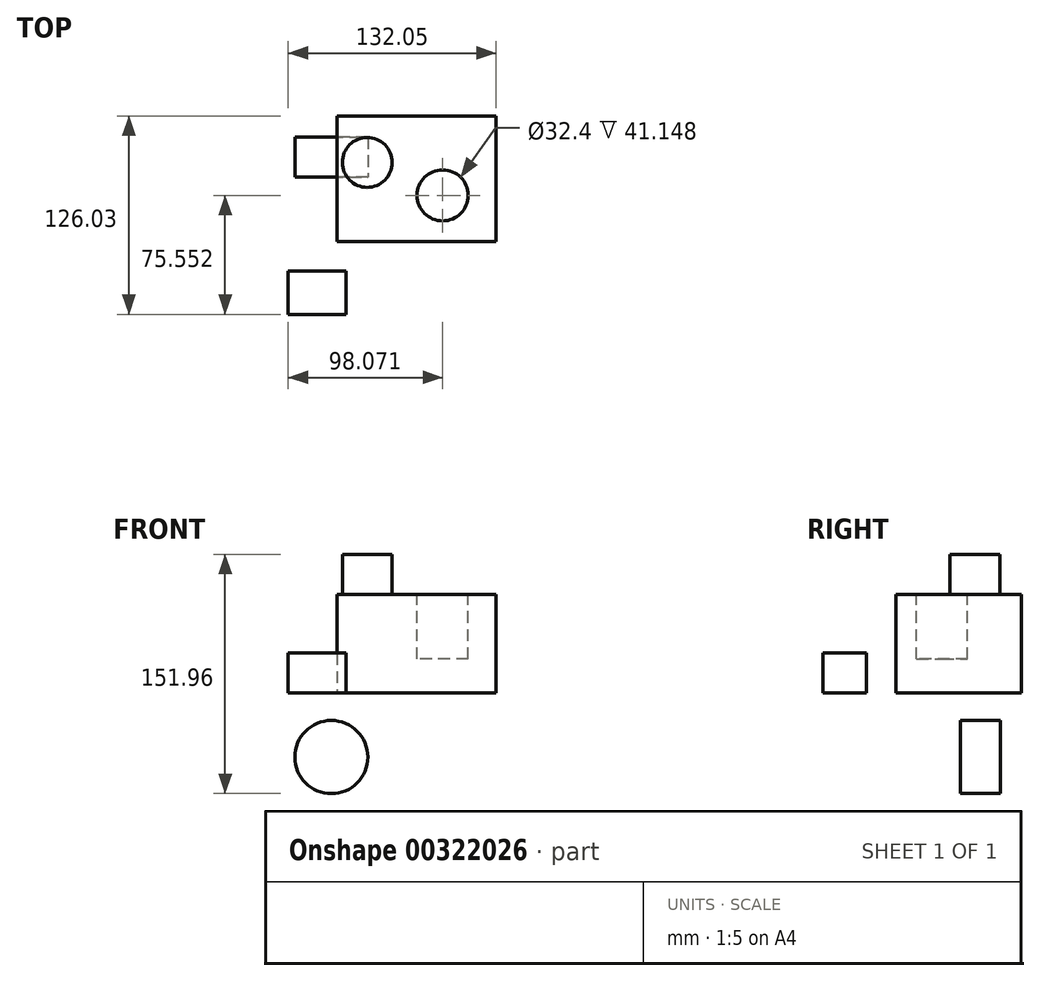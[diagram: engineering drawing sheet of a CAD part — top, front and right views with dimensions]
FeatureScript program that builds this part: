
annotation { "Feature Type Name" : "Feature", "Feature Type Description" : "" }
export const myFeature = defineFeature(function(context is Context, id is Id, definition is map)
    precondition{}
    {
        {
            var Q0;
            Q0=qCreatedBy(makeId("Top.planeOp"),FACE);
            var sketch = newSketch(context, id + "F0", { "sketchPlane" : qUnion([Q0])});
            skLineSegment(sketch, "E0.bottom", {"start": v(-39.24, 38.83) * mm, "end": v(61.89, 38.83) * mm});
            skLineSegment(sketch, "E0.top", {"start": v(-39.24, -40.85) * mm, "end": v(61.89, -40.85) * mm});
            skLineSegment(sketch, "E0.left", {"start": v(-39.24, 38.83) * mm, "end": v(-39.24, -40.85) * mm});
            skLineSegment(sketch, "E0.right", {"start": v(61.89, 38.83) * mm, "end": v(61.89, -40.85) * mm});
            skSolve(sketch);
        }
        {
            var Q0;
            Q0=makeQuery(id+"F0.imprint","IMPRINT",FACE,{"disambiguationData":[TD([[makeQuery(id+"F0.imprint","IMPRINT",EDGE,{"derivedFrom":sQuery(id+"F0.wireOp",EDGE,"E0.bottom")}),-1.0]])]});
            extrude(context, id + "F1", {"entities" : qUnion([Q0]), "depth" : 62.74 * mm});
        }
        {
            var Q0;
            Q0=makeQuery(id+"F1.opExtrude","CAP_FACE",FACE,{"disambiguationData":[OSD([sQuery(id+"F0.wireOp",EDGE,"E0.bottom"),sQuery(id+"F0.wireOp",EDGE,"E0.top"),sQuery(id+"F0.wireOp",EDGE,"E0.left"),sQuery(id+"F0.wireOp",EDGE,"E0.right")])],"isStart":false});
            var sketch = newSketch(context, id + "F2", { "sketchPlane" : qUnion([Q0])});
            skCircle(sketch, "E1", {"center": v(27.91, -11.65) * mm, "radius": 16.2 * mm});
            skSolve(sketch);
        }
        {
            var Q0;
            Q0=makeQuery(id+"F2.imprint","IMPRINT",FACE,{"disambiguationData":[TD([[makeQuery(id+"F2.imprint","IMPRINT",EDGE,{"derivedFrom":sQuery(id+"F2.wireOp",EDGE,"E1")}),1.0]])]});
            extrude(context, id + "F3", {"entities" : qUnion([Q0]), "operationType" : NewBodyOperationType.REMOVE, "oppositeDirection" : true, "depth" : 41.15 * mm});
        }
        {
            var Q0;
            Q0=qCreatedBy(makeId("Top.planeOp"),FACE);
            var sketch = newSketch(context, id + "F4", { "sketchPlane" : qUnion([Q0])});
            skLineSegment(sketch, "E2.bottom", {"start": v(-70.16, -87.2) * mm, "end": v(-33.46, -87.2) * mm});
            skLineSegment(sketch, "E2.top", {"start": v(-70.16, -59.59) * mm, "end": v(-33.46, -59.59) * mm});
            skLineSegment(sketch, "E2.left", {"start": v(-70.16, -87.2) * mm, "end": v(-70.16, -59.59) * mm});
            skLineSegment(sketch, "E2.right", {"start": v(-33.46, -87.2) * mm, "end": v(-33.46, -59.59) * mm});
            skSolve(sketch);
        }
        {
            var Q0;
            Q0 = qSketchRegion(id + "F4", true);
            extrude(context, id + "F5", {"entities" : qUnion([Q0]), "depth" : 25.4 * mm});
        }
        {
            var Q0;
            Q0=qCreatedBy(makeId("Front.planeOp"),FACE);
            var sketch = newSketch(context, id + "F6", { "sketchPlane" : qUnion([Q0])});
            skCircle(sketch, "E3", {"center": v(-42.75, -40.6) * mm, "radius": 23.23 * mm});
            skSolve(sketch);
        }
        {
            var Q0;
            Q0 = qSketchRegion(id + "F6", true);
            extrude(context, id + "F7", {"entities" : qUnion([Q0]), "oppositeDirection" : true, "depth" : 25.4 * mm});
        }
        {
            var Q0;
            Q0=makeQuery(id+"F1.opExtrude","CAP_FACE",FACE,{"disambiguationData":[OSD([sQuery(id+"F0.wireOp",EDGE,"E0.bottom"),sQuery(id+"F0.wireOp",EDGE,"E0.top"),sQuery(id+"F0.wireOp",EDGE,"E0.left"),sQuery(id+"F0.wireOp",EDGE,"E0.right")])],"isStart":false});
            var sketch = newSketch(context, id + "F8", { "sketchPlane" : qUnion([Q0])});
            skCircle(sketch, "E4", {"center": v(-19.99, 9.26) * mm, "radius": 15.82 * mm});
            skSolve(sketch);
        }
        {
            var Q0;
            Q0 = qSketchRegion(id + "F8", true);
            extrude(context, id + "F9", {"entities" : qUnion([Q0]), "depth" : 25.4 * mm});
        }
    });
